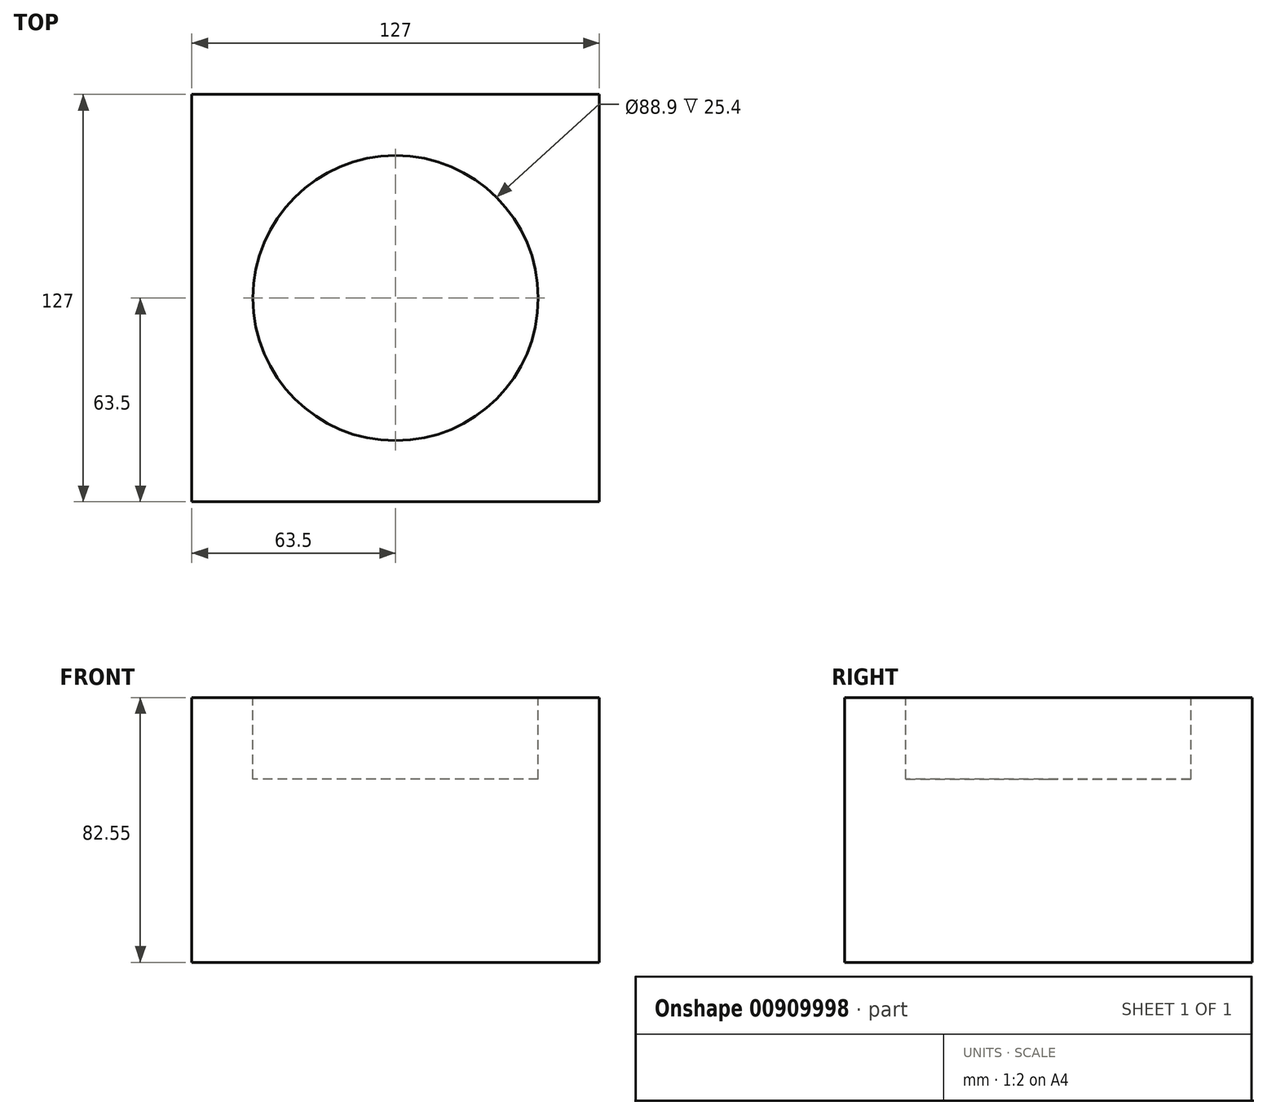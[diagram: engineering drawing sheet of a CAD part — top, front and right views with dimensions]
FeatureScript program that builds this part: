
annotation { "Feature Type Name" : "Feature", "Feature Type Description" : "" }
export const myFeature = defineFeature(function(context is Context, id is Id, definition is map)
    precondition{}
    {
        {
            var Q0;
            Q0=qCreatedBy(makeId("Front.planeOp"),FACE);
            var sketch = newSketch(context, id + "F0", { "sketchPlane" : qUnion([Q0])});
            skLineSegment(sketch, "E0.bottom", {"start": v(-63.5, 82.55) * mm, "end": v(63.5, 82.55) * mm});
            skLineSegment(sketch, "E0.top", {"start": v(-63.5, 0) * mm, "end": v(63.5, 0) * mm});
            skLineSegment(sketch, "E0.left", {"start": v(-63.5, 82.55) * mm, "end": v(-63.5, 0) * mm});
            skLineSegment(sketch, "E0.right", {"start": v(63.5, 82.55) * mm, "end": v(63.5, 0) * mm});
            skLineSegment(sketch, "E1", {"start": v(0, 0) * mm, "end": v(0, 82.55) * mm, "construction": true});
            skLineSegment(sketch, "E2", {"start": v(0, 82.55) * mm, "end": v(0, 57.15) * mm});
            skLineSegment(sketch, "E3", {"start": v(0, 57.15) * mm, "end": v(44.45, 57.15) * mm});
            skLineSegment(sketch, "E4", {"start": v(44.45, 57.15) * mm, "end": v(44.45, 82.55) * mm});
            skSolve(sketch);
        }
        {
            var Q0;
            Q0=makeQuery(id+"F0.imprint","IMPRINT",FACE,{"disambiguationData":[TD([[makeQuery(id+"F0.imprint","IMPRINT",EDGE,{"derivedFrom":sQuery(id+"F0.wireOp",EDGE,"E0.bottom")}),-1.0]])]});
            var Q1;
            {var subQ0=sQuery(id+"F0.wireOp",EDGE,"E2");Q1=makeQuery(id+"F0.imprint","IMPRINT",FACE,{"disambiguationData":[TD([[makeQuery(id+"F0.imprint","IMPRINT",EDGE,{"derivedFrom":subQ0}),1.0]])]});}
            extrude(context, id + "F1", {"entities" : qUnion([Q0, Q1]), "depth" : 127 * mm, "offsetDistance" : 25 * mm, "symmetric" : true});
        }
        {
            var Q0;
            {var subQ0=sQuery(id+"F0.wireOp",EDGE,"E2");Q0=makeQuery(id+"F0.imprint","IMPRINT",FACE,{"disambiguationData":[TD([[makeQuery(id+"F0.imprint","IMPRINT",EDGE,{"derivedFrom":subQ0}),1.0]])]});}
            var Q1;
            Q1=sQuery(id+"F0.wireOp",EDGE,"E1");
            revolve(context, id + "F2", {"operationType" : NewBodyOperationType.REMOVE, "surfaceOperationType" : NewSurfaceOperationType.NEW, "entities" : qUnion([Q0]), "axis" : qUnion([Q1]), "revolveType" : RevolveType.FULL, "oppositeDirection" : true});
        }
    });
